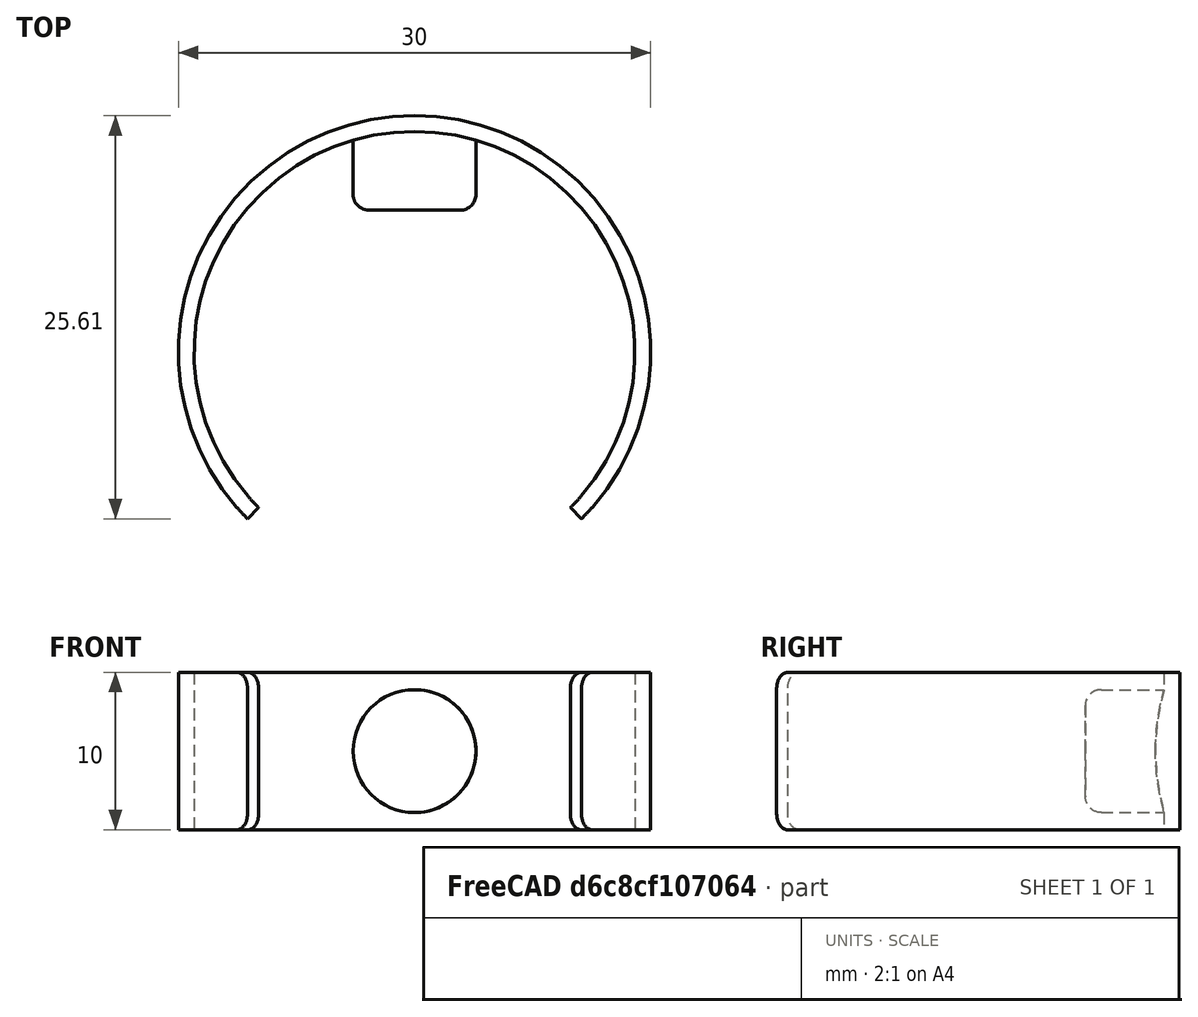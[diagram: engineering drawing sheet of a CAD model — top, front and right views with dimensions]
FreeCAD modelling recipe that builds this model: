
FCSTD DOCUMENT  (FreeCAD 0.20R29603 (Git))
Label: rogzito_csat
License: All rights reserved
LicenseURL: http://en.wikipedia.org/wiki/All_rights_reserved
objects: PartDesign::AdditiveCylinder×2, PartDesign::Fillet×2, PartDesign::SubtractiveCylinder×1, PartDesign::Body×1
note: 11 computed .brp shape members not serialized (recipe doc carries the construction recipe); baked Part::Feature solids carry a one-line shape summary decoded from their .brp

FEATURE [PartDesign::AdditiveCylinder] Cylinder
  Angle = 270
  AttacherType = Attacher::AttachEngine3D
  AttachmentOffset = pos=(0,0,0) rot=(0,0,-1;0.785398rad)
  FirstAngle = 0
  Height = 10
  MapMode = 5
  Placement = pos=(0,0,0) rot=(0,0,-1;0.785398rad)
  Radius = 15
  SecondAngle = 0
  Support = -> [XY_Plane]
FEATURE [PartDesign::SubtractiveCylinder] Cylinder001
  Angle = 270
  AttacherType = Attacher::AttachEngine3D
  AttachmentOffset = pos=(0,0,0) rot=(0,0,-1;0.785398rad)
  BaseFeature = -> Cylinder
  FirstAngle = 0
  Height = 10
  MapMode = 5
  Placement = pos=(0,0,0) rot=(0,0,-1;0.785398rad)
  Radius = 14
  SecondAngle = 0
  Support = -> [XY_Plane]
FEATURE [PartDesign::AdditiveCylinder] Cylinder002
  Angle = 360
  AttacherType = Attacher::AttachEngine3D
  AttachmentOffset = pos=(0,5,-14) rot=(0,0,1;0rad)
  BaseFeature = -> Cylinder001
  FirstAngle = 0
  Height = 5
  MapMode = 5
  Placement = pos=(0,14,5) rot=(1,0,0;1.5708rad)
  Radius = 3.9
  SecondAngle = 0
  Support = -> [XZ_Plane]
FEATURE [PartDesign::Fillet] Fillet
  Base = -> Cylinder002 [Edge17]
  BaseFeature = -> Cylinder002
  Placement = pos=(0,14,5) rot=(1,0,0;1.5708rad)
  Radius = 1
  SupportTransform = false
  UseAllEdges = false
FEATURE [PartDesign::Fillet] Fillet001
  Base = -> Fillet [Edge14,Edge12,Edge16,Edge18]
  BaseFeature = -> Fillet
  Placement = pos=(0,14,5) rot=(1,0,0;1.5708rad)
  Radius = 1
  SupportTransform = false
  UseAllEdges = false
FEATURE [PartDesign::Body] Body
  Group = -> [Cylinder,Cylinder001,Cylinder002,Fillet,Fillet001]
  Origin = -> Origin
  Tip = -> Fillet001
